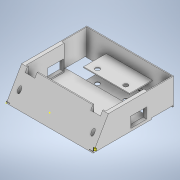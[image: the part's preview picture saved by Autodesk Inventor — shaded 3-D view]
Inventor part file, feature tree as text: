
AUTODESK INVENTOR PART (.ipt)
format: ipt  version: 2021 (Build 250183000, 183)  size: 432,128 bytes
history: native  units: mm
features: sketch x21, extrude x18, projected_geometry x2, other x1
ambient origin geometry x8: Origin, YZ Plane, XZ Plane, XY Plane, X Axis, Y Axis, Z Axis, Center Point
bodies: Body1 (feature_tree)
feature tree (42):
  other  "Sólido1"
  extrude  "Extrusion Base"  Depth=1.5mm TaperAngle=0.0deg
  extrude  "Extrusión Angulo parte de adelante"  Depth=100.0mm TaperAngle=0.0deg
  extrude  "Grado de inclinacion de 60.5 de parte delantera"  Depth=4.0mm TaperAngle=0.0deg
  extrude  "Lateral derecha de diseño"  Depth=103.25mm TaperAngle=0.0deg
  extrude  "Lateral izquierda diseño"  Depth=93.0mm
  extrude  "Extrusion capa parte delantera"  Depth=3.5mm
  extrude  "Extrusión huecos tornillos parte delantera"  Depth=3.0mm
  extrude  "Extrusión sensores laterales"  Depth=12.0mm
  extrude  "Extrusión arreglo sensores"  Depth=63.5mm
  extrude  "Extrusión desnivel sensores"  Depth=84.0mm
  sketch  "Boceto placa"  dims[d235=1.0mm d236=3.6mm d239=2.1mm d241=1.3mm d242=5.0mm d243=36.0mm d244=9.5mm d245=5.0mm d246=17.0mm d247=10.0mm d252=8.7mm d254=4.3mm d255=4.0mm d256=11.0mm d257=54.0mm d258=2.85mm d259=11.0mm d262=2.2mm d263=1.3mm d264=4.3mm d265=85.25mm d266=0.0mm d268=2.0mm d269=0.0mm d270=2.15mm d271=1.0mm d278=1.0mm d279=0.0mm d281=28.5mm d282=1.0mm d283=0.0mm d284=28.5mm d285=1.0mm d286=0.0mm d289=3.0mm d290=0.0mm d291=1.0mm d292=0.0mm d293=13.5mm d294=1.0mm d295=0.0mm d296=0.0mm d297=25.75mm d298=0.0mm d299=25.75mm d300=0.0mm d301=2.0mm d302=0.0mm d105=0.5mm d106=0.872665mm d107=0.5mm d108=0.872665mm d248=0.5mm d249=0.872665mm d250=0.5mm d251=0.872665mm d253=0.872665mm d272=0.5mm d273=0.872665mm d303=0.5mm d304=0.872665mm]
  extrude  "Extrusión35"  Depth=10.0mm
  extrude  "Extrusión36"  Depth=35.5mm
  extrude  "Extrusión37"  TaperAngle=0.0deg  [1 undecoded]
  sketch  "Boceto52"  dims[d178=3.5mm d179=35.5mm]
  extrude  "Extrusión39"  Depth=21.0mm
  sketch  "Boceto54"  dims[d219=87.0mm d220=21.0mm]
  extrude  "Extrusión40"  Depth=23.0mm
  extrude  "Extrusión41"  Depth=98.0mm
  extrude  "Extrusión42"  Depth=79.5mm
  sketch  "Boceto58"  dims[d229=2.1mm d230=9.0mm]
  sketch  "Boceto59"  dims[d231=11.0mm]
  extrude  "Extrusión43"  Depth=2.1mm
  sketch  "Boceto2"  dims[d6=3.5mm d22=1.5mm d23=0.0mm]
  sketch  "Boceto4"  dims[d24=20.935224mm d25=100.0mm d26=0.0mm]
  sketch  "Boceto10"  dims[d52=4.0mm d53=0.0mm d54=4.0mm d55=0.0mm]
  sketch  "Boceto11"  dims[d59=10.480702mm d60=103.25mm d61=0.0mm]
  projected_geometry  "Contorno proyectado1"
  sketch  "Boceto15"  dims[d65=93.0mm d66=0.0mm d67=7.5mm]
  projected_geometry  "Contorno proyectado2"
  sketch  "Boceto17"  dims[d68=7.5mm d69=3.5mm]
  sketch  "Boceto39"  dims[d70=90.25mm d71=0.0mm d131=3.0mm]
  sketch  "Boceto40"  dims[d132=18.0mm d133=12.0mm]
  sketch  "Boceto48"  dims[d134=98.25mm d135=0.0mm d167=63.5mm]
  sketch  "Boceto49"  dims[d168=26.5mm d172=84.0mm]
  sketch  "Boceto50"  dims[d176=10.0mm d177=3.993mm]
  sketch  "Boceto53"  dims[d180=9.069006mm d210=0.0mm]
  sketch  "Boceto55"  dims[d221=12.0mm d222=23.0mm]
  sketch  "Boceto56"  dims[d223=98.0mm d224=7.5mm]
  sketch  "Boceto57"  dims[d225=7.5mm d226=79.5mm]
  sketch  "Boceto60"  dims[d232=16.0mm]
note: 1 required parameter value undecoded (feature->parameter linkage not recoverable at this tier; creation-order binding heuristic only, values carry confidence <= 0.55)
